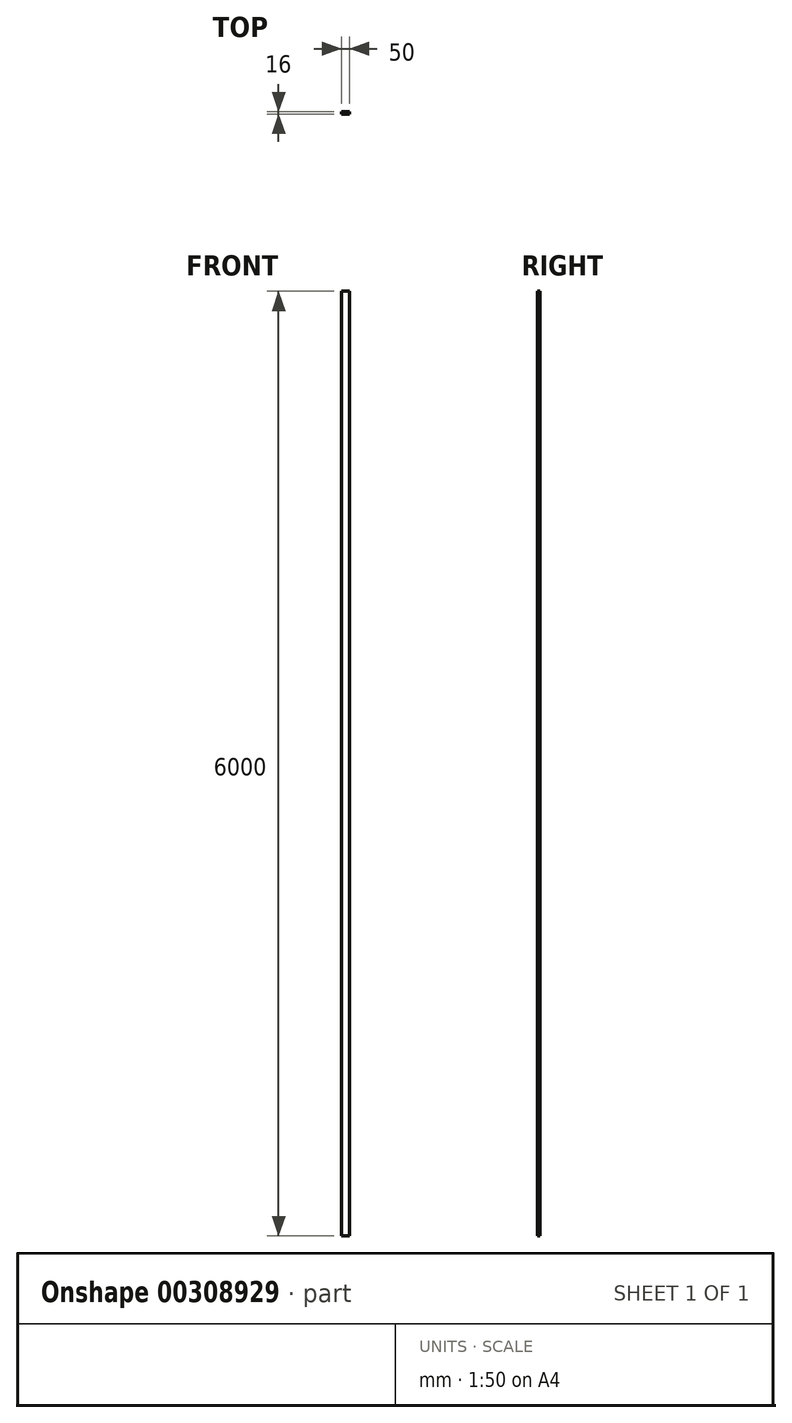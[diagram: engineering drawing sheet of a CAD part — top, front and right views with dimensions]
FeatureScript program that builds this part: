
annotation { "Feature Type Name" : "Feature", "Feature Type Description" : "" }
export const myFeature = defineFeature(function(context is Context, id is Id, definition is map)
    precondition{}
    {
        {
            var Q0;
            Q0=qCreatedBy(makeId("Top.planeOp"),FACE);
            var sketch = newSketch(context, id + "F0", { "sketchPlane" : qUnion([Q0])});
            skLineSegment(sketch, "E0.bottom", {"start": v(25, -8) * mm, "end": v(-25, -8) * mm});
            skLineSegment(sketch, "E0.top", {"start": v(25, 8) * mm, "end": v(-25, 8) * mm});
            skLineSegment(sketch, "E0.left", {"start": v(25, -8) * mm, "end": v(25, 8) * mm});
            skLineSegment(sketch, "E0.right", {"start": v(-25, -8) * mm, "end": v(-25, 8) * mm});
            skPoint(sketch, "E0.middle", {"position": v(0, 0) * mm});
            skSolve(sketch);
        }
        {
            var Q0;
            Q0=qSketchRegion(id+"F0",true);
            extrude(context, id + "F1", {"entities" : qUnion([Q0]), "depth" : 6000 * mm});
        }
    });
